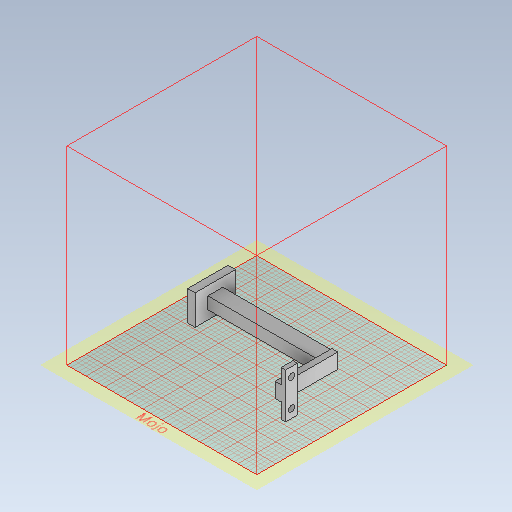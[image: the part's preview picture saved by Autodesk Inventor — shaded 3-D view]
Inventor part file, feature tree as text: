
AUTODESK INVENTOR PART (.ipt)
format: ipt  version: 2020 (Build 240168000, 168)  size: 336,896 bytes
history: native  units: mm
features: sketch x7, extrude x6, other x1, hole x1
ambient origin geometry x8: Origin, YZ Plane, XZ Plane, XY Plane, X Axis, Y Axis, Z Axis, Center Point
bodies: Body1 (feature_tree)
feature tree (15):
  other  "솔리드1"
  extrude  "돌출1"  Depth=20.0mm
  extrude  "돌출2"  Depth=27.0mm
  extrude  "돌출3"  Depth=5.0mm TaperAngle=0.0deg
  extrude  "돌출4"  Depth=8.0mm
  extrude  "돌출6"  Depth=10.0mm
  hole  "구멍1"  [1 undecoded]
  extrude  "돌출7"  Depth=10.0mm
  sketch  "스케치1"
  sketch  "스케치2"
  sketch  "스케치3"
  sketch  "스케치4"
  sketch  "스케치6"
  sketch  "스케치7"
  sketch  "스케치8"
note: 1 required parameter value undecoded (feature->parameter linkage not recoverable at this tier; creation-order binding heuristic only, values carry confidence <= 0.55)
